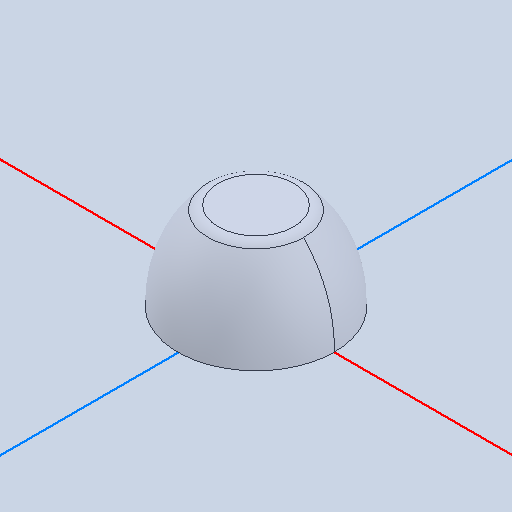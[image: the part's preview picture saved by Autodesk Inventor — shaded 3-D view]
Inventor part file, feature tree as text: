
AUTODESK INVENTOR PART (.ipt)
format: ipt  version: 2022 (Build 260153000, 153)  size: 138,752 bytes
history: native  units: mm
features: other x1, fillet x1
ambient origin geometry x8: Origin, YZ Plane, XZ Plane, XY Plane, X Axis, Y Axis, Z Axis, Center Point
bodies: Body1 (feature_tree)
feature tree (2):
  other  "Твердое тело1"
  fillet  "Fillet1"  [1 undecoded]
note: 1 required parameter value undecoded (feature->parameter linkage not recoverable at this tier; creation-order binding heuristic only, values carry confidence <= 0.55)
